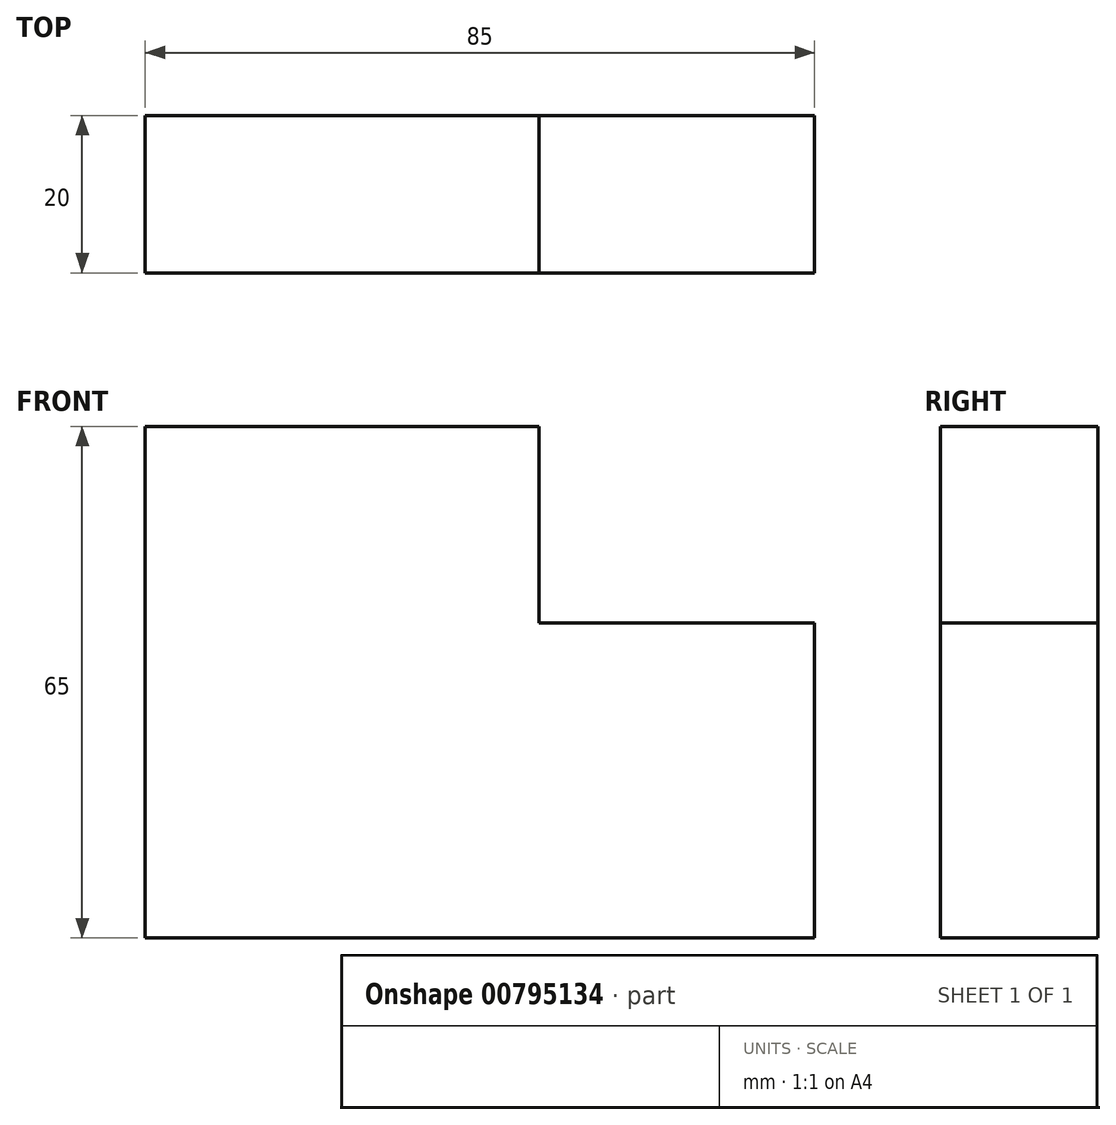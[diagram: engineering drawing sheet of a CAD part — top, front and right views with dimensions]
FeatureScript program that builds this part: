
annotation { "Feature Type Name" : "Feature", "Feature Type Description" : "" }
export const myFeature = defineFeature(function(context is Context, id is Id, definition is map)
    precondition{}
    {
        {
            var Q0;
            Q0=qCreatedBy(makeId("Front.planeOp"),FACE);
            var sketch = newSketch(context, id + "F0", { "sketchPlane" : qUnion([Q0])});
            skLineSegment(sketch, "E0", {"start": v(-42.5, 32.5) * mm, "end": v(7.5, 32.5) * mm});
            skLineSegment(sketch, "E1", {"start": v(7.5, 32.5) * mm, "end": v(7.5, 7.5) * mm});
            skLineSegment(sketch, "E2", {"start": v(7.5, 7.5) * mm, "end": v(42.5, 7.5) * mm});
            skLineSegment(sketch, "E3", {"start": v(42.5, 7.5) * mm, "end": v(42.5, -32.5) * mm});
            skLineSegment(sketch, "E4", {"start": v(42.5, -32.5) * mm, "end": v(-42.5, -32.5) * mm});
            skLineSegment(sketch, "E5", {"start": v(-42.5, -32.5) * mm, "end": v(-42.5, 32.5) * mm});
            skLineSegment(sketch, "E6", {"start": v(-42.5, 0) * mm, "end": v(42.5, 0) * mm, "construction": true});
            skPoint(sketch, "E7", {"position": v(0, 0) * mm});
            skSolve(sketch);
        }
        {
            var Q0;
            Q0=makeQuery(id+"F0.imprint","IMPRINT",FACE,{"disambiguationData":[TD([[makeQuery(id+"F0.imprint","IMPRINT",EDGE,{"derivedFrom":sQuery(id+"F0.wireOp",EDGE,"E0")}),-1.0]])]});
            extrude(context, id + "F1", {"entities" : qUnion([Q0]), "endBound" : BoundingType.SYMMETRIC, "depth" : 20 * mm, "offsetDistance" : 25 * mm});
        }
    });
